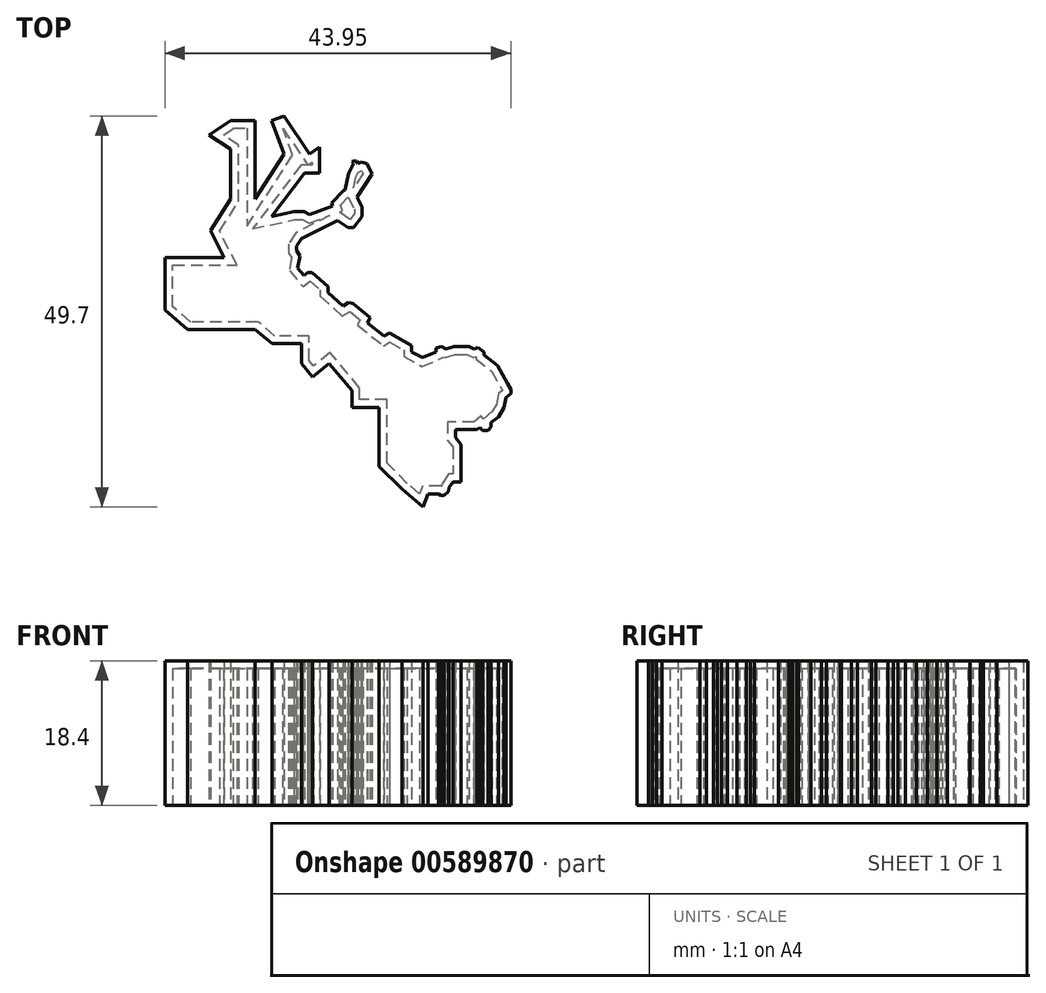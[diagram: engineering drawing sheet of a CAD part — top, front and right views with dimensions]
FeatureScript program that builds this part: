
annotation { "Feature Type Name" : "Feature", "Feature Type Description" : "" }
export const myFeature = defineFeature(function(context is Context, id is Id, definition is map)
    precondition{}
    {
        {
            var Q0;
            Q0=qCreatedBy(makeId("Top.planeOp"),FACE);
            var sketch = newSketch(context, id + "F0", { "sketchPlane" : qUnion([Q0])});
            skLineSegment(sketch, "E0", {"start": v(37.6, 0) * mm, "end": v(34.9, 2.3) * mm});
            skLineSegment(sketch, "E1", {"start": v(34.9, 2.3) * mm, "end": v(32.02, 5.2) * mm});
            skLineSegment(sketch, "E2", {"start": v(32.02, 5.2) * mm, "end": v(32.02, 12.7) * mm});
            skLineSegment(sketch, "E3", {"start": v(32.02, 12.7) * mm, "end": v(28.56, 12.7) * mm});
            skLineSegment(sketch, "E4", {"start": v(28.56, 12.7) * mm, "end": v(28.56, 14.8) * mm});
            skLineSegment(sketch, "E5", {"start": v(28.56, 14.8) * mm, "end": v(25.67, 18.27) * mm});
            skLineSegment(sketch, "E6", {"start": v(25.67, 18.27) * mm, "end": v(23.6, 16.54) * mm});
            skLineSegment(sketch, "E7", {"start": v(23.6, 16.54) * mm, "end": v(22.15, 18.27) * mm});
            skLineSegment(sketch, "E8", {"start": v(22.15, 18.27) * mm, "end": v(22.15, 20.77) * mm});
            skLineSegment(sketch, "E9", {"start": v(22.15, 20.77) * mm, "end": v(20.56, 20.77) * mm});
            skLineSegment(sketch, "E10", {"start": v(20.56, 20.77) * mm, "end": v(18.4, 20.77) * mm});
            skLineSegment(sketch, "E11", {"start": v(18.4, 20.77) * mm, "end": v(16.28, 22.55) * mm});
            skLineSegment(sketch, "E12", {"start": v(16.28, 22.55) * mm, "end": v(11.42, 22.55) * mm});
            skLineSegment(sketch, "E13", {"start": v(11.42, 22.55) * mm, "end": v(7.7, 22.55) * mm});
            skLineSegment(sketch, "E14", {"start": v(7.7, 22.55) * mm, "end": v(4.81, 25.02) * mm});
            skLineSegment(sketch, "E15", {"start": v(4.81, 25.02) * mm, "end": v(4.81, 28.7) * mm});
            skLineSegment(sketch, "E16", {"start": v(4.81, 28.7) * mm, "end": v(4.81, 31.74) * mm});
            skLineSegment(sketch, "E17", {"start": v(4.81, 31.74) * mm, "end": v(8.62, 31.74) * mm});
            skLineSegment(sketch, "E18", {"start": v(8.62, 31.74) * mm, "end": v(12.32, 31.74) * mm});
            skLineSegment(sketch, "E19", {"start": v(12.32, 31.74) * mm, "end": v(10.6, 35.13) * mm});
            skLineSegment(sketch, "E20", {"start": v(10.6, 35.13) * mm, "end": v(13.18, 39.13) * mm});
            skLineSegment(sketch, "E21", {"start": v(13.18, 39.13) * mm, "end": v(13.18, 45.48) * mm});
            skLineSegment(sketch, "E22", {"start": v(13.18, 45.48) * mm, "end": v(10.43, 47.26) * mm});
            skLineSegment(sketch, "E23", {"start": v(10.43, 47.26) * mm, "end": v(13.18, 49.13) * mm});
            skLineSegment(sketch, "E24", {"start": v(13.18, 49.13) * mm, "end": v(16.24, 49.13) * mm});
            skLineSegment(sketch, "E25", {"start": v(16.24, 49.13) * mm, "end": v(16.24, 44.87) * mm});
            skLineSegment(sketch, "E26", {"start": v(16.24, 44.87) * mm, "end": v(16.24, 39.13) * mm});
            skLineSegment(sketch, "E27", {"start": v(16.24, 39.13) * mm, "end": v(19.94, 44.87) * mm});
            skLineSegment(sketch, "E28", {"start": v(19.94, 44.87) * mm, "end": v(18.38, 49.13) * mm});
            skLineSegment(sketch, "E29", {"start": v(18.38, 49.13) * mm, "end": v(19.94, 49.7) * mm});
            skLineSegment(sketch, "E30", {"start": v(19.94, 49.7) * mm, "end": v(23.21, 44.87) * mm});
            skLineSegment(sketch, "E31", {"start": v(23.21, 44.87) * mm, "end": v(24.48, 45.72) * mm});
            skLineSegment(sketch, "E32", {"start": v(24.48, 45.72) * mm, "end": v(24.48, 42.44) * mm});
            skLineSegment(sketch, "E33", {"start": v(24.48, 42.44) * mm, "end": v(22.58, 42.44) * mm});
            skLineSegment(sketch, "E34", {"start": v(22.58, 42.44) * mm, "end": v(18.38, 36.93) * mm});
            skLineSegment(sketch, "E35", {"start": v(18.38, 36.93) * mm, "end": v(21.2, 37.54) * mm});
            skLineSegment(sketch, "E36", {"start": v(21.2, 37.54) * mm, "end": v(22.5, 37.54) * mm});
            skLineSegment(sketch, "E37", {"start": v(22.5, 37.54) * mm, "end": v(23.2, 37.2) * mm});
            skLineSegment(sketch, "E38", {"start": v(23.2, 37.2) * mm, "end": v(26.1, 38.23) * mm});
            skLineSegment(sketch, "E39", {"start": v(26.1, 38.23) * mm, "end": v(25.96, 38.63) * mm});
            skLineSegment(sketch, "E40", {"start": v(25.96, 38.63) * mm, "end": v(27.5, 40.2) * mm});
            skLineSegment(sketch, "E41", {"start": v(27.5, 40.2) * mm, "end": v(27.67, 40.28) * mm});
            skLineSegment(sketch, "E42", {"start": v(27.67, 40.28) * mm, "end": v(28.12, 42.36) * mm});
            skLineSegment(sketch, "E43", {"start": v(28.12, 42.36) * mm, "end": v(28.76, 43.64) * mm});
            skLineSegment(sketch, "E44", {"start": v(28.76, 43.64) * mm, "end": v(28.61, 43.92) * mm});
            skLineSegment(sketch, "E45", {"start": v(28.61, 43.92) * mm, "end": v(28.76, 44) * mm});
            skLineSegment(sketch, "E46", {"start": v(28.76, 44) * mm, "end": v(29.14, 44) * mm});
            skLineSegment(sketch, "E47", {"start": v(29.14, 44) * mm, "end": v(29.33, 43.64) * mm});
            skLineSegment(sketch, "E48", {"start": v(29.33, 43.64) * mm, "end": v(29.74, 43.85) * mm});
            skLineSegment(sketch, "E49", {"start": v(29.74, 43.85) * mm, "end": v(30.47, 43.64) * mm});
            skLineSegment(sketch, "E50", {"start": v(30.47, 43.64) * mm, "end": v(31.14, 42.31) * mm});
            skLineSegment(sketch, "E51", {"start": v(31.14, 42.31) * mm, "end": v(29.2, 39.42) * mm});
            skLineSegment(sketch, "E52", {"start": v(29.2, 39.42) * mm, "end": v(29.87, 38.1) * mm});
            skLineSegment(sketch, "E53", {"start": v(29.87, 38.1) * mm, "end": v(29.87, 36.93) * mm});
            skLineSegment(sketch, "E54", {"start": v(29.87, 36.93) * mm, "end": v(28.76, 35.51) * mm});
            skLineSegment(sketch, "E55", {"start": v(28.76, 35.51) * mm, "end": v(28.05, 35.51) * mm});
            skLineSegment(sketch, "E56", {"start": v(28.05, 35.51) * mm, "end": v(26.75, 36.44) * mm});
            skLineSegment(sketch, "E57", {"start": v(26.75, 36.44) * mm, "end": v(22.15, 34.1) * mm});
            skLineSegment(sketch, "E58", {"start": v(22.15, 34.1) * mm, "end": v(21.52, 33.16) * mm});
            skLineSegment(sketch, "E59", {"start": v(21.52, 33.16) * mm, "end": v(21.52, 32.58) * mm});
            skLineSegment(sketch, "E60", {"start": v(21.52, 32.58) * mm, "end": v(21.95, 31.92) * mm});
            skLineSegment(sketch, "E61", {"start": v(21.95, 31.92) * mm, "end": v(21.69, 30.36) * mm});
            skLineSegment(sketch, "E62", {"start": v(21.69, 30.36) * mm, "end": v(22.48, 29.43) * mm});
            skLineSegment(sketch, "E63", {"start": v(22.48, 29.43) * mm, "end": v(22.93, 29.82) * mm});
            skLineSegment(sketch, "E64", {"start": v(22.93, 29.82) * mm, "end": v(23.52, 29.82) * mm});
            skLineSegment(sketch, "E65", {"start": v(23.52, 29.82) * mm, "end": v(25.53, 28.04) * mm});
            skLineSegment(sketch, "E66", {"start": v(25.53, 28.04) * mm, "end": v(25.53, 27.27) * mm});
            skLineSegment(sketch, "E67", {"start": v(25.53, 27.27) * mm, "end": v(27.44, 25.52) * mm});
            skLineSegment(sketch, "E68", {"start": v(27.44, 25.52) * mm, "end": v(28.15, 25.97) * mm});
            skLineSegment(sketch, "E69", {"start": v(28.15, 25.97) * mm, "end": v(28.7, 25.84) * mm});
            skLineSegment(sketch, "E70", {"start": v(28.7, 25.84) * mm, "end": v(30.84, 24.09) * mm});
            skLineSegment(sketch, "E71", {"start": v(30.84, 24.09) * mm, "end": v(30.53, 23.42) * mm});
            skLineSegment(sketch, "E72", {"start": v(30.53, 23.42) * mm, "end": v(32.68, 21.72) * mm});
            skLineSegment(sketch, "E73", {"start": v(32.68, 21.72) * mm, "end": v(33.35, 22.12) * mm});
            skLineSegment(sketch, "E74", {"start": v(33.35, 22.12) * mm, "end": v(36.16, 20.54) * mm});
            skLineSegment(sketch, "E75", {"start": v(36.16, 20.54) * mm, "end": v(36.16, 19.74) * mm});
            skLineSegment(sketch, "E76", {"start": v(36.16, 19.74) * mm, "end": v(37.53, 18.99) * mm});
            skLineSegment(sketch, "E77", {"start": v(37.53, 18.99) * mm, "end": v(39.26, 19.74) * mm});
            skLineSegment(sketch, "E78", {"start": v(39.26, 19.74) * mm, "end": v(39.26, 20.25) * mm});
            skLineSegment(sketch, "E79", {"start": v(39.26, 20.25) * mm, "end": v(39.95, 20.4) * mm});
            skLineSegment(sketch, "E80", {"start": v(39.95, 20.4) * mm, "end": v(40.5, 20.07) * mm});
            skLineSegment(sketch, "E81", {"start": v(40.5, 20.07) * mm, "end": v(41.53, 20.4) * mm});
            skLineSegment(sketch, "E82", {"start": v(41.53, 20.4) * mm, "end": v(43.43, 20.4) * mm});
            skLineSegment(sketch, "E83", {"start": v(43.43, 20.4) * mm, "end": v(44.05, 20.11) * mm});
            skLineSegment(sketch, "E84", {"start": v(44.05, 20.11) * mm, "end": v(44.6, 20.31) * mm});
            skLineSegment(sketch, "E85", {"start": v(44.6, 20.31) * mm, "end": v(45.33, 19.74) * mm});
            skLineSegment(sketch, "E86", {"start": v(45.33, 19.74) * mm, "end": v(45.33, 19.34) * mm});
            skLineSegment(sketch, "E87", {"start": v(45.33, 19.34) * mm, "end": v(47.07, 17.98) * mm});
            skLineSegment(sketch, "E88", {"start": v(47.07, 17.98) * mm, "end": v(48.33, 15.73) * mm});
            skLineSegment(sketch, "E89", {"start": v(48.33, 15.73) * mm, "end": v(48.76, 14.97) * mm});
            skLineSegment(sketch, "E90", {"start": v(48.76, 14.97) * mm, "end": v(48.76, 14.44) * mm});
            skLineSegment(sketch, "E91", {"start": v(48.76, 14.44) * mm, "end": v(48.12, 13.9) * mm});
            skLineSegment(sketch, "E92", {"start": v(48.12, 13.9) * mm, "end": v(47.88, 12.7) * mm});
            skLineSegment(sketch, "E93", {"start": v(47.88, 12.7) * mm, "end": v(47.16, 11.49) * mm});
            skLineSegment(sketch, "E94", {"start": v(47.16, 11.49) * mm, "end": v(46.26, 10.74) * mm});
            skLineSegment(sketch, "E95", {"start": v(46.26, 10.74) * mm, "end": v(46.26, 10.21) * mm});
            skLineSegment(sketch, "E96", {"start": v(46.26, 10.21) * mm, "end": v(45.88, 9.73) * mm});
            skLineSegment(sketch, "E97", {"start": v(45.88, 9.73) * mm, "end": v(45.18, 9.73) * mm});
            skLineSegment(sketch, "E98", {"start": v(45.18, 9.73) * mm, "end": v(44.82, 10.16) * mm});
            skLineSegment(sketch, "E99", {"start": v(44.82, 10.16) * mm, "end": v(44.46, 9.85) * mm});
            skLineSegment(sketch, "E100", {"start": v(44.46, 9.85) * mm, "end": v(41.7, 9.85) * mm});
            skLineSegment(sketch, "E101", {"start": v(41.7, 9.85) * mm, "end": v(41.7, 8.84) * mm});
            skLineSegment(sketch, "E102", {"start": v(41.7, 8.84) * mm, "end": v(42.41, 7.99) * mm});
            skLineSegment(sketch, "E103", {"start": v(42.41, 7.99) * mm, "end": v(42.41, 5.58) * mm});
            skLineSegment(sketch, "E104", {"start": v(42.41, 5.58) * mm, "end": v(42.41, 3.97) * mm});
            skLineSegment(sketch, "E105", {"start": v(42.41, 3.97) * mm, "end": v(42.41, 3.22) * mm});
            skLineSegment(sketch, "E106", {"start": v(42.41, 3.22) * mm, "end": v(41.38, 3.22) * mm});
            skLineSegment(sketch, "E107", {"start": v(41.38, 3.22) * mm, "end": v(40.93, 2.52) * mm});
            skLineSegment(sketch, "E108", {"start": v(40.93, 2.52) * mm, "end": v(40.86, 1.97) * mm});
            skLineSegment(sketch, "E109", {"start": v(40.86, 1.97) * mm, "end": v(40.26, 1.47) * mm});
            skLineSegment(sketch, "E110", {"start": v(40.26, 1.47) * mm, "end": v(39.86, 1.47) * mm});
            skLineSegment(sketch, "E111", {"start": v(39.86, 1.47) * mm, "end": v(39.55, 1.68) * mm});
            skLineSegment(sketch, "E112", {"start": v(39.55, 1.68) * mm, "end": v(38.22, 1.68) * mm});
            skLineSegment(sketch, "E113", {"start": v(38.22, 1.68) * mm, "end": v(37.6, 0) * mm});
            skSolve(sketch);
        }
        {
            var Q0;
            Q0=makeQuery(id+"F0.imprint","IMPRINT",FACE,{"disambiguationData":[TD([[makeQuery(id+"F0.imprint","IMPRINT",EDGE,{"derivedFrom":sQuery(id+"F0.wireOp",EDGE,"E0")}),-1.0]])]});
            extrude(context, id + "F1", {"entities" : qUnion([Q0]), "depth" : 18.4 * mm, "offsetDistance" : 25 * mm});
        }
        {
            var Q0;
            Q0=makeQuery(id+"F1.opExtrude","CAP_FACE",FACE,{"disambiguationData":[OSD([sQuery(id+"F0.wireOp",EDGE,"E0"),sQuery(id+"F0.wireOp",EDGE,"E1"),sQuery(id+"F0.wireOp",EDGE,"E2"),sQuery(id+"F0.wireOp",EDGE,"E3"),sQuery(id+"F0.wireOp",EDGE,"E4"),sQuery(id+"F0.wireOp",EDGE,"E5"),sQuery(id+"F0.wireOp",EDGE,"E6"),sQuery(id+"F0.wireOp",EDGE,"E7"),sQuery(id+"F0.wireOp",EDGE,"E8"),sQuery(id+"F0.wireOp",EDGE,"E9"),sQuery(id+"F0.wireOp",EDGE,"E10"),sQuery(id+"F0.wireOp",EDGE,"E11"),sQuery(id+"F0.wireOp",EDGE,"E12"),sQuery(id+"F0.wireOp",EDGE,"E13"),sQuery(id+"F0.wireOp",EDGE,"E14"),sQuery(id+"F0.wireOp",EDGE,"E15"),sQuery(id+"F0.wireOp",EDGE,"E16"),sQuery(id+"F0.wireOp",EDGE,"E17"),sQuery(id+"F0.wireOp",EDGE,"E18"),sQuery(id+"F0.wireOp",EDGE,"E19"),sQuery(id+"F0.wireOp",EDGE,"E20"),sQuery(id+"F0.wireOp",EDGE,"E21"),sQuery(id+"F0.wireOp",EDGE,"E22"),sQuery(id+"F0.wireOp",EDGE,"E23"),sQuery(id+"F0.wireOp",EDGE,"E24"),sQuery(id+"F0.wireOp",EDGE,"E25"),sQuery(id+"F0.wireOp",EDGE,"E26"),sQuery(id+"F0.wireOp",EDGE,"E27"),sQuery(id+"F0.wireOp",EDGE,"E28"),sQuery(id+"F0.wireOp",EDGE,"E29"),sQuery(id+"F0.wireOp",EDGE,"E30"),sQuery(id+"F0.wireOp",EDGE,"E31"),sQuery(id+"F0.wireOp",EDGE,"E32"),sQuery(id+"F0.wireOp",EDGE,"E33"),sQuery(id+"F0.wireOp",EDGE,"E34"),sQuery(id+"F0.wireOp",EDGE,"E35"),sQuery(id+"F0.wireOp",EDGE,"E36"),sQuery(id+"F0.wireOp",EDGE,"E37"),sQuery(id+"F0.wireOp",EDGE,"E38"),sQuery(id+"F0.wireOp",EDGE,"E39"),sQuery(id+"F0.wireOp",EDGE,"E40"),sQuery(id+"F0.wireOp",EDGE,"E41"),sQuery(id+"F0.wireOp",EDGE,"E42"),sQuery(id+"F0.wireOp",EDGE,"E43"),sQuery(id+"F0.wireOp",EDGE,"E44"),sQuery(id+"F0.wireOp",EDGE,"E45"),sQuery(id+"F0.wireOp",EDGE,"E46"),sQuery(id+"F0.wireOp",EDGE,"E47"),sQuery(id+"F0.wireOp",EDGE,"E48"),sQuery(id+"F0.wireOp",EDGE,"E49"),sQuery(id+"F0.wireOp",EDGE,"E50"),sQuery(id+"F0.wireOp",EDGE,"E51"),sQuery(id+"F0.wireOp",EDGE,"E52"),sQuery(id+"F0.wireOp",EDGE,"E53"),sQuery(id+"F0.wireOp",EDGE,"E54"),sQuery(id+"F0.wireOp",EDGE,"E55"),sQuery(id+"F0.wireOp",EDGE,"E56"),sQuery(id+"F0.wireOp",EDGE,"E57"),sQuery(id+"F0.wireOp",EDGE,"E58"),sQuery(id+"F0.wireOp",EDGE,"E59"),sQuery(id+"F0.wireOp",EDGE,"E60"),sQuery(id+"F0.wireOp",EDGE,"E61"),sQuery(id+"F0.wireOp",EDGE,"E62"),sQuery(id+"F0.wireOp",EDGE,"E63"),sQuery(id+"F0.wireOp",EDGE,"E64"),sQuery(id+"F0.wireOp",EDGE,"E65"),sQuery(id+"F0.wireOp",EDGE,"E66"),sQuery(id+"F0.wireOp",EDGE,"E67"),sQuery(id+"F0.wireOp",EDGE,"E68"),sQuery(id+"F0.wireOp",EDGE,"E69"),sQuery(id+"F0.wireOp",EDGE,"E70"),sQuery(id+"F0.wireOp",EDGE,"E71"),sQuery(id+"F0.wireOp",EDGE,"E72"),sQuery(id+"F0.wireOp",EDGE,"E73"),sQuery(id+"F0.wireOp",EDGE,"E74"),sQuery(id+"F0.wireOp",EDGE,"E75"),sQuery(id+"F0.wireOp",EDGE,"E76"),sQuery(id+"F0.wireOp",EDGE,"E77"),sQuery(id+"F0.wireOp",EDGE,"E78"),sQuery(id+"F0.wireOp",EDGE,"E79"),sQuery(id+"F0.wireOp",EDGE,"E80"),sQuery(id+"F0.wireOp",EDGE,"E81"),sQuery(id+"F0.wireOp",EDGE,"E82"),sQuery(id+"F0.wireOp",EDGE,"E83"),sQuery(id+"F0.wireOp",EDGE,"E84"),sQuery(id+"F0.wireOp",EDGE,"E85"),sQuery(id+"F0.wireOp",EDGE,"E86"),sQuery(id+"F0.wireOp",EDGE,"E87"),sQuery(id+"F0.wireOp",EDGE,"E88"),sQuery(id+"F0.wireOp",EDGE,"E89"),sQuery(id+"F0.wireOp",EDGE,"E90"),sQuery(id+"F0.wireOp",EDGE,"E91"),sQuery(id+"F0.wireOp",EDGE,"E92"),sQuery(id+"F0.wireOp",EDGE,"E93"),sQuery(id+"F0.wireOp",EDGE,"E94"),sQuery(id+"F0.wireOp",EDGE,"E95"),sQuery(id+"F0.wireOp",EDGE,"E96"),sQuery(id+"F0.wireOp",EDGE,"E97"),sQuery(id+"F0.wireOp",EDGE,"E98"),sQuery(id+"F0.wireOp",EDGE,"E99"),sQuery(id+"F0.wireOp",EDGE,"E100"),sQuery(id+"F0.wireOp",EDGE,"E101"),sQuery(id+"F0.wireOp",EDGE,"E102"),sQuery(id+"F0.wireOp",EDGE,"E103"),sQuery(id+"F0.wireOp",EDGE,"E104"),sQuery(id+"F0.wireOp",EDGE,"E105"),sQuery(id+"F0.wireOp",EDGE,"E106"),sQuery(id+"F0.wireOp",EDGE,"E107"),sQuery(id+"F0.wireOp",EDGE,"E108"),sQuery(id+"F0.wireOp",EDGE,"E109"),sQuery(id+"F0.wireOp",EDGE,"E110"),sQuery(id+"F0.wireOp",EDGE,"E111"),sQuery(id+"F0.wireOp",EDGE,"E112"),sQuery(id+"F0.wireOp",EDGE,"E113")])],"isStart":true});
            shell(context, id + "F2", {"entities" : qUnion([Q0]), "thickness" : 1 * mm});
        }
    });
